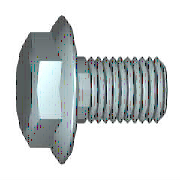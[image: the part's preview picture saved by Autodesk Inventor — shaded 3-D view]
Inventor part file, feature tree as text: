
AUTODESK INVENTOR PART (.ipt)
format: ipt  version: 2022 (Build 260153000, 153)  size: 202,240 bytes
history: native  units: mm (DEFAULTED — no unit token found)
features: sketch x3, extrude x1, chamfer x1, plane x1
ambient origin geometry x7: Origin, YZ Plane, XZ Plane, X Axis, Y Axis, Z Axis, Center Point
bodies: Solid1 (feature_tree), Body (feature_tree)
feature tree (6):
  extrude  "Head"  Depth=70.0mm
  chamfer  "Chamfer1"  Distance=8.0mm
  plane  "Work Plane1"
  sketch  "Sketch1"  dims[d0=1.2mm d1=70.0mm]
  sketch  "Sketch2"  dims[d2=22.0mm]
  sketch  "Sketch3"  dims[d3=17.0mm d4=8.0mm d5=3.825mm d12=90.0deg d6=8.5mm d7=0.0mm d8=30.0deg d21=90.0deg d10=22.0mm d11=0.0mm d13=0.766813mm d14=0.766813mm d15=8.0mm d16=8.0mm d17=0.0001mm d18=0.766813mm d19=4.363323mm d20=0.0mm d22=9.5mm d23=10.0mm d39=45.0deg d40=0.0mm d41=0.0mm]
